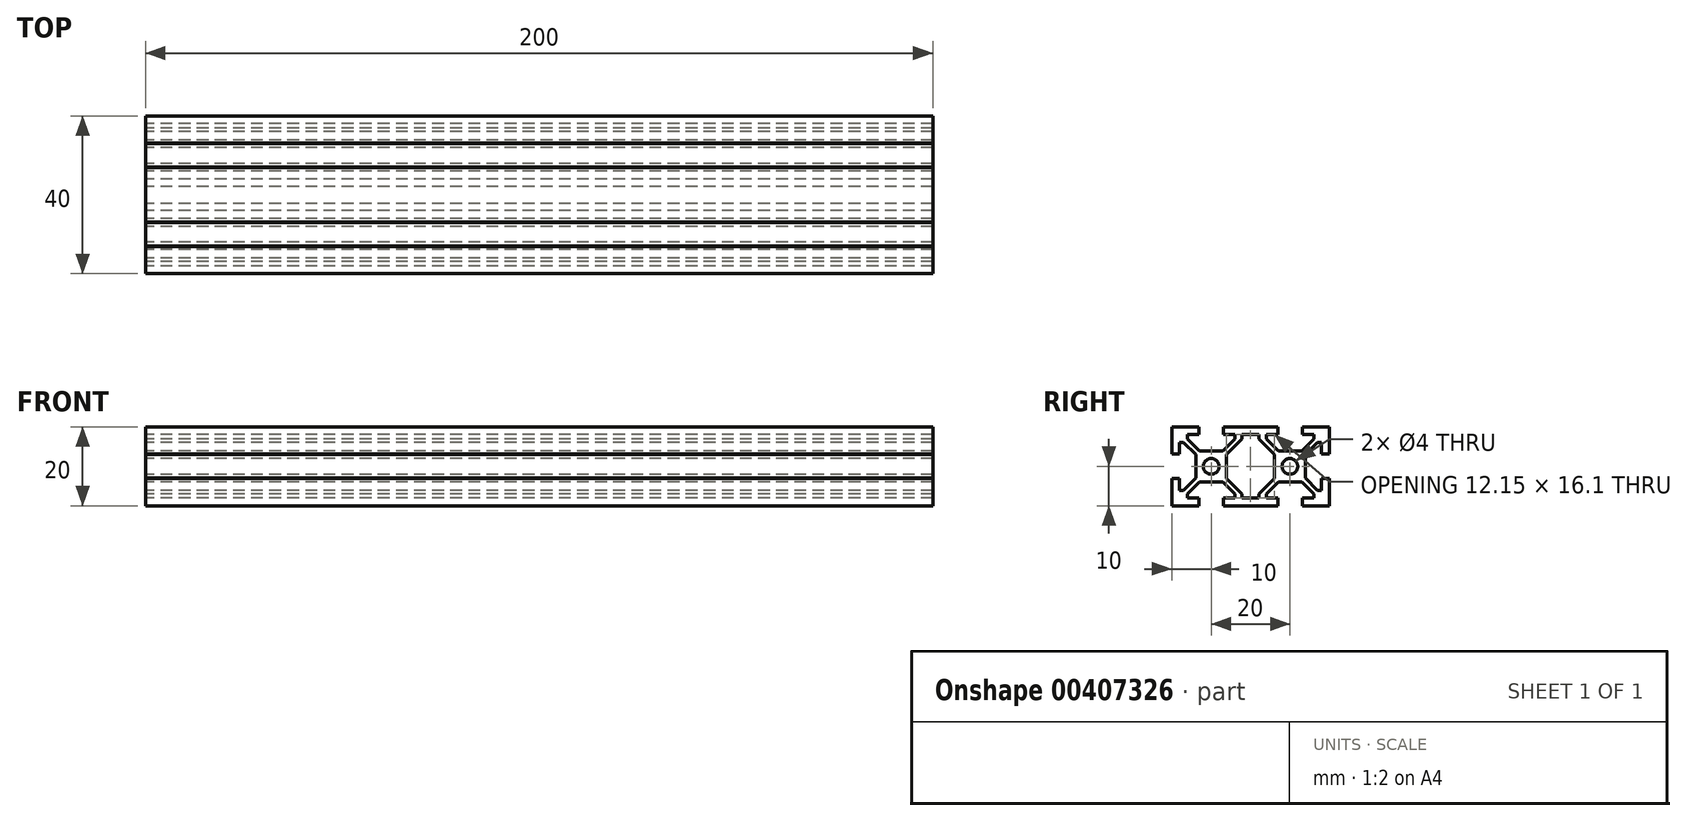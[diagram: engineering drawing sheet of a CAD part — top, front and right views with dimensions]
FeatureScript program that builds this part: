
annotation { "Feature Type Name" : "Feature", "Feature Type Description" : "" }
export const myFeature = defineFeature(function(context is Context, id is Id, definition is map)
    precondition{}
    {
        {
            var Q0;
            Q0=qCreatedBy(makeId("Right.planeOp"),FACE);
            var sketch = newSketch(context, id + "F0", { "sketchPlane" : qUnion([Q0])});
            skLineSegment(sketch, "E0", {"start": v(0, 0) * mm, "end": v(0, 10) * mm, "construction": true});
            skLineSegment(sketch, "E1", {"start": v(0, 10) * mm, "end": v(-6.93, 10) * mm});
            skLineSegment(sketch, "E2", {"start": v(-6.93, 10) * mm, "end": v(-6.93, 8.05) * mm});
            skLineSegment(sketch, "E3", {"start": v(-6.93, 8.05) * mm, "end": v(-4, 8.05) * mm});
            skLineSegment(sketch, "E4", {"start": v(-4, 8.05) * mm, "end": v(-4, 7) * mm});
            skLineSegment(sketch, "E5", {"start": v(-4, 7) * mm, "end": v(-7.07, 3.93) * mm});
            skLineSegment(sketch, "E6", {"start": v(-16.08, 7) * mm, "end": v(-13, 3.93) * mm});
            skLineSegment(sketch, "E7", {"start": v(-16.08, 7) * mm, "end": v(-16.08, 8.05) * mm});
            skLineSegment(sketch, "E8", {"start": v(-16.08, 8.05) * mm, "end": v(-13.12, 8.05) * mm});
            skLineSegment(sketch, "E9", {"start": v(-13.12, 8.05) * mm, "end": v(-13.12, 10) * mm});
            skLineSegment(sketch, "E10", {"start": v(-13.12, 10) * mm, "end": v(-20, 10) * mm});
            skLineSegment(sketch, "E11", {"start": v(-20, 10) * mm, "end": v(-20, 3.12) * mm});
            skLineSegment(sketch, "E12", {"start": v(-20, 3.12) * mm, "end": v(-18.05, 3.12) * mm});
            skLineSegment(sketch, "E13", {"start": v(-18.05, 3.12) * mm, "end": v(-18.05, 6.08) * mm});
            skLineSegment(sketch, "E14", {"start": v(-18.05, 6.08) * mm, "end": v(-17, 6.08) * mm});
            skLineSegment(sketch, "E15", {"start": v(-13.93, 3) * mm, "end": v(-17, 6.08) * mm});
            skLineSegment(sketch, "E16", {"start": v(-13.92, 3) * mm, "end": v(-13.92, 0) * mm});
            skLineSegment(sketch, "E17", {"start": v(0, 0) * mm, "end": v(-13.92, 0) * mm, "construction": true});
            skLineSegment(sketch, "E18.MirrorCS", {"start": v(18.05, 6.08) * mm, "end": v(17, 6.08) * mm});
            skLineSegment(sketch, "E19.MirrorCS", {"start": v(0, 10) * mm, "end": v(6.93, 10) * mm});
            skLineSegment(sketch, "E20.MirrorCS", {"start": v(13.93, 3) * mm, "end": v(17, 6.08) * mm});
            skLineSegment(sketch, "E21.MirrorCS", {"start": v(18.05, 3.12) * mm, "end": v(18.05, 6.08) * mm});
            skLineSegment(sketch, "E22.MirrorCS", {"start": v(13.93, 3) * mm, "end": v(13.93, 0) * mm});
            skLineSegment(sketch, "E23.MirrorCS", {"start": v(6.94, 10) * mm, "end": v(6.94, 8.05) * mm});
            skLineSegment(sketch, "E24.MirrorCS", {"start": v(20, 3.12) * mm, "end": v(18.05, 3.12) * mm});
            skLineSegment(sketch, "E25.MirrorCS", {"start": v(6.94, 8.05) * mm, "end": v(4, 8.05) * mm});
            skLineSegment(sketch, "E26.MirrorCS", {"start": v(20, 10) * mm, "end": v(20, 3.12) * mm});
            skLineSegment(sketch, "E27.MirrorCS", {"start": v(13.12, 10) * mm, "end": v(20, 10) * mm});
            skLineSegment(sketch, "E28.MirrorCS", {"start": v(13.12, 8.05) * mm, "end": v(13.12, 10) * mm});
            skLineSegment(sketch, "E29.MirrorCS", {"start": v(7.07, 3.93) * mm, "end": v(13, 3.93) * mm});
            skLineSegment(sketch, "E30.MirrorCS", {"start": v(4, 8.05) * mm, "end": v(4, 7) * mm});
            skLineSegment(sketch, "E31.MirrorCS", {"start": v(16.08, 7) * mm, "end": v(16.08, 8.05) * mm});
            skLineSegment(sketch, "E32.MirrorCS", {"start": v(4, 7) * mm, "end": v(7.07, 3.93) * mm});
            skLineSegment(sketch, "E33.MirrorCS", {"start": v(16.08, 7) * mm, "end": v(13, 3.93) * mm});
            skLineSegment(sketch, "E34.MirrorCS", {"start": v(16.08, 8.05) * mm, "end": v(13.12, 8.05) * mm});
            skLineSegment(sketch, "E35.MirrorCS", {"start": v(18.05, -6.08) * mm, "end": v(17, -6.08) * mm});
            skLineSegment(sketch, "E36.MirrorCS", {"start": v(-18.05, -6.08) * mm, "end": v(-17, -6.08) * mm});
            skLineSegment(sketch, "E37.MirrorCS", {"start": v(-13.92, -3) * mm, "end": v(-17, -6.08) * mm});
            skLineSegment(sketch, "E38.MirrorCS", {"start": v(13.12, -8.05) * mm, "end": v(13.12, -10) * mm});
            skLineSegment(sketch, "E39.MirrorCS", {"start": v(0, -10) * mm, "end": v(6.94, -10) * mm});
            skLineSegment(sketch, "E40.MirrorCS", {"start": v(4, -8.05) * mm, "end": v(4, -7) * mm});
            skLineSegment(sketch, "E41.MirrorCS", {"start": v(18.05, -3.12) * mm, "end": v(18.05, -6.08) * mm});
            skLineSegment(sketch, "E42.MirrorCS", {"start": v(20, -10) * mm, "end": v(20, -3.12) * mm});
            skLineSegment(sketch, "E43.MirrorCS", {"start": v(-20, -10) * mm, "end": v(-20, -3.12) * mm});
            skLineSegment(sketch, "E44.MirrorCS", {"start": v(-13.12, -10) * mm, "end": v(-20, -10) * mm});
            skLineSegment(sketch, "E45.MirrorCS", {"start": v(13.12, -10) * mm, "end": v(20, -10) * mm});
            skLineSegment(sketch, "E46.MirrorCS", {"start": v(-13.12, -8.05) * mm, "end": v(-13.12, -10) * mm});
            skLineSegment(sketch, "E47.MirrorCS", {"start": v(-16.08, -8.05) * mm, "end": v(-13.12, -8.05) * mm});
            skLineSegment(sketch, "E48.MirrorCS", {"start": v(-16.08, -7) * mm, "end": v(-16.08, -8.05) * mm});
            skLineSegment(sketch, "E49.MirrorCS", {"start": v(-7.07, -3.93) * mm, "end": v(-13, -3.93) * mm});
            skLineSegment(sketch, "E50.MirrorCS", {"start": v(6.94, -8.05) * mm, "end": v(4, -8.05) * mm});
            skLineSegment(sketch, "E51.MirrorCS", {"start": v(6.93, -10) * mm, "end": v(6.93, -8.05) * mm});
            skLineSegment(sketch, "E52.MirrorCS", {"start": v(-4, -7) * mm, "end": v(-7.07, -3.93) * mm});
            skLineSegment(sketch, "E53.MirrorCS", {"start": v(-4, -8.05) * mm, "end": v(-4, -7) * mm});
            skLineSegment(sketch, "E54.MirrorCS", {"start": v(-6.93, -8.05) * mm, "end": v(-4, -8.05) * mm});
            skLineSegment(sketch, "E55.MirrorCS", {"start": v(-6.93, -10) * mm, "end": v(-6.93, -8.05) * mm});
            skLineSegment(sketch, "E56.MirrorCS", {"start": v(13.93, -3) * mm, "end": v(17, -6.08) * mm});
            skLineSegment(sketch, "E57.MirrorCS", {"start": v(7.07, -3.93) * mm, "end": v(13, -3.93) * mm});
            skLineSegment(sketch, "E58.MirrorCS", {"start": v(4, -7) * mm, "end": v(7.07, -3.93) * mm});
            skLineSegment(sketch, "E59.MirrorCS", {"start": v(16.08, -7) * mm, "end": v(13, -3.92) * mm});
            skLineSegment(sketch, "E60.MirrorCS", {"start": v(16.08, -7) * mm, "end": v(16.08, -8.05) * mm});
            skLineSegment(sketch, "E61.MirrorCS", {"start": v(20, -3.12) * mm, "end": v(18.05, -3.12) * mm});
            skLineSegment(sketch, "E62.MirrorCS", {"start": v(-20, -3.12) * mm, "end": v(-18.05, -3.12) * mm});
            skLineSegment(sketch, "E63.MirrorCS", {"start": v(0, 0) * mm, "end": v(0, -10) * mm, "construction": true});
            skLineSegment(sketch, "E64.MirrorCS", {"start": v(0, -10) * mm, "end": v(-6.93, -10) * mm});
            skLineSegment(sketch, "E65.MirrorCS", {"start": v(13.93, -3) * mm, "end": v(13.93, 0) * mm});
            skLineSegment(sketch, "E66.MirrorCS", {"start": v(-16.08, -7) * mm, "end": v(-13, -3.93) * mm});
            skLineSegment(sketch, "E67.MirrorCS", {"start": v(-13.92, -3) * mm, "end": v(-13.92, 0) * mm});
            skLineSegment(sketch, "E68.MirrorCS", {"start": v(-18.05, -3.12) * mm, "end": v(-18.05, -6.08) * mm});
            skLineSegment(sketch, "E69.MirrorCS", {"start": v(16.08, -8.05) * mm, "end": v(13.12, -8.05) * mm});
            skLineSegment(sketch, "E70", {"start": v(-13, 3.93) * mm, "end": v(-7.07, 3.93) * mm});
            skLineSegment(sketch, "E71", {"start": v(-20, 10) * mm, "end": v(-10, 0) * mm, "construction": true});
            skLineSegment(sketch, "E72", {"start": v(0, 8.05) * mm, "end": v(-2.16, 8.05) * mm});
            skLineSegment(sketch, "E73", {"start": v(-2.16, 8.05) * mm, "end": v(-2.16, 7) * mm});
            skLineSegment(sketch, "E74", {"start": v(-2.16, 7) * mm, "end": v(-6.08, 3.09) * mm});
            skLineSegment(sketch, "E75", {"start": v(-6.08, 3.09) * mm, "end": v(-6.08, 0) * mm});
            skLineSegment(sketch, "E76.MirrorCS", {"start": v(0, 8.05) * mm, "end": v(2.16, 8.05) * mm});
            skLineSegment(sketch, "E77.MirrorCS", {"start": v(2.16, 8.05) * mm, "end": v(2.16, 7) * mm});
            skLineSegment(sketch, "E78.MirrorCS", {"start": v(2.16, 7) * mm, "end": v(6.08, 3.09) * mm});
            skLineSegment(sketch, "E79.MirrorCS", {"start": v(6.08, 3.09) * mm, "end": v(6.08, 0) * mm});
            skLineSegment(sketch, "E80.MirrorCS", {"start": v(-2.16, -7) * mm, "end": v(-6.07, -3.09) * mm});
            skLineSegment(sketch, "E81.MirrorCS", {"start": v(-6.07, -3.09) * mm, "end": v(-6.08, 0) * mm});
            skLineSegment(sketch, "E82.MirrorCS", {"start": v(-2.16, -8.05) * mm, "end": v(-2.16, -7) * mm});
            skLineSegment(sketch, "E83.MirrorCS", {"start": v(0, -8.05) * mm, "end": v(-2.16, -8.05) * mm});
            skLineSegment(sketch, "E84.MirrorCS", {"start": v(0, -8.05) * mm, "end": v(2.16, -8.05) * mm});
            skLineSegment(sketch, "E85.MirrorCS", {"start": v(2.16, -8.05) * mm, "end": v(2.16, -7) * mm});
            skLineSegment(sketch, "E86.MirrorCS", {"start": v(2.16, -7) * mm, "end": v(6.08, -3.09) * mm});
            skLineSegment(sketch, "E87.MirrorCS", {"start": v(6.08, -3.09) * mm, "end": v(6.08, 0) * mm});
            skLineSegment(sketch, "E88", {"start": v(-16.08, 7) * mm, "end": v(-4, 7) * mm, "construction": true});
            skLineSegment(sketch, "E89", {"start": v(-10, 0) * mm, "end": v(0, 10) * mm, "construction": true});
            skCircle(sketch, "E90", {"center": v(-10, 0) * mm, "radius": 2 * mm});
            skCircle(sketch, "E91.MirrorC", {"center": v(10, 0) * mm, "radius": 2 * mm});
            skSolve(sketch);
        }
        {
            var Q0;
            Q0=makeQuery(id+"F0.imprint","IMPRINT",FACE,{"disambiguationData":[TD([[makeQuery(id+"F0.imprint","IMPRINT",EDGE,{"derivedFrom":sQuery(id+"F0.wireOp",EDGE,"E1")}),1.0]])]});
            extrude(context, id + "F1", {"entities" : qUnion([Q0]), "depth" : 200 * mm});
        }
    });
